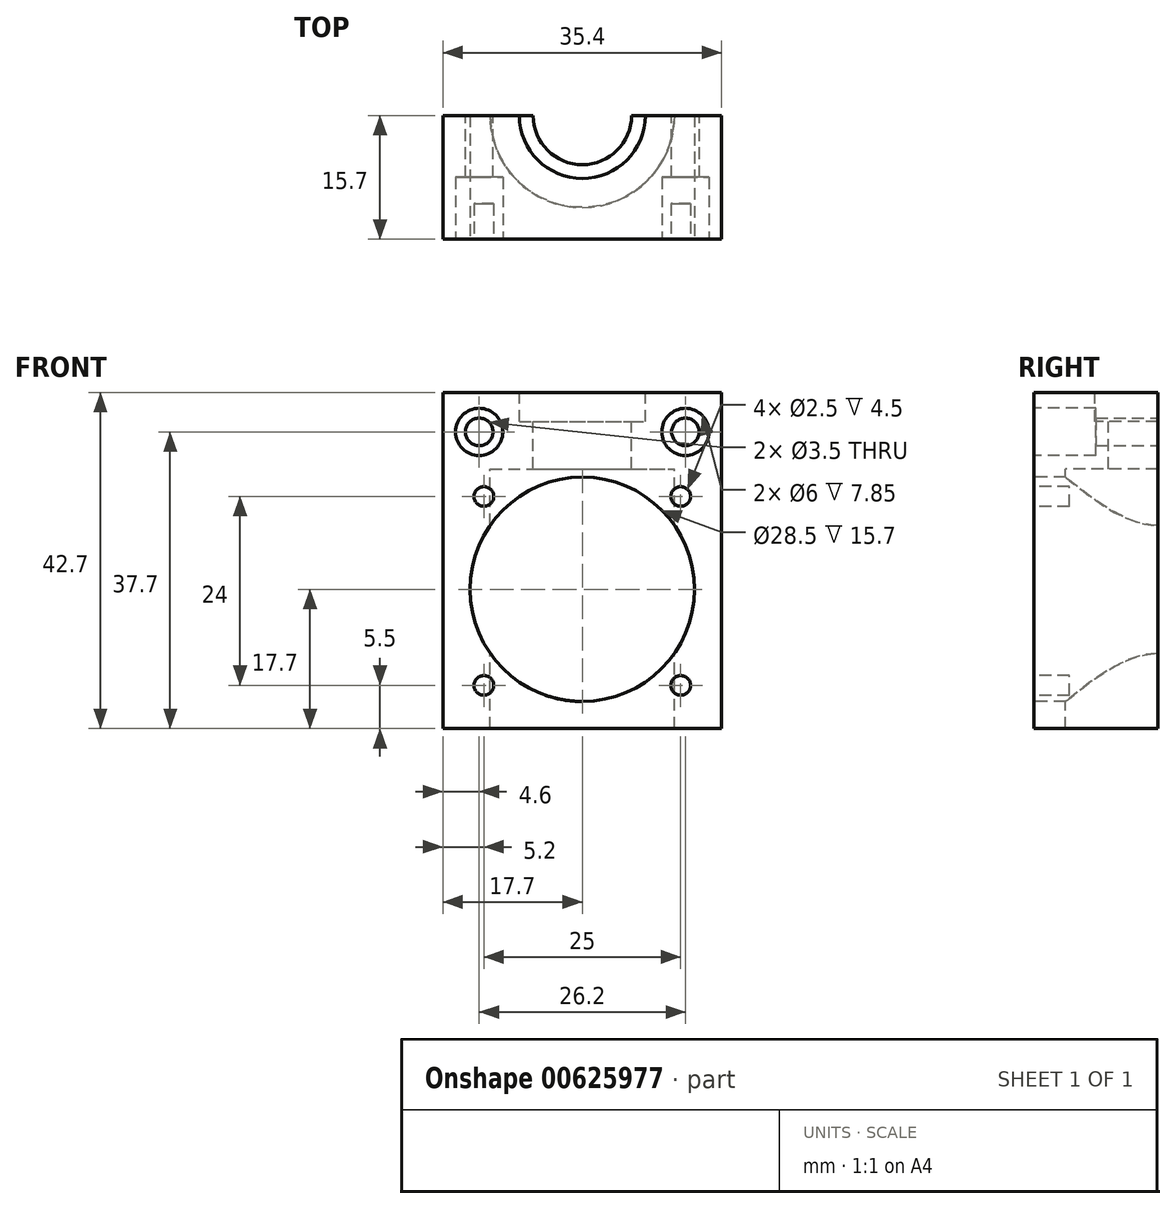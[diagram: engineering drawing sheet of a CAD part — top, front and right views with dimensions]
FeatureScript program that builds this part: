
annotation { "Feature Type Name" : "Feature", "Feature Type Description" : "" }
export const myFeature = defineFeature(function(context is Context, id is Id, definition is map)
    precondition{}
    {
        {
            var Q0;
            Q0=qCreatedBy(makeId("Top.planeOp"),FACE);
            var sketch = newSketch(context, id + "F0", { "sketchPlane" : qUnion([Q0])});
            skLineSegment(sketch, "E0.bottom", {"start": v(0, 0) * mm, "end": v(35.4, 0) * mm});
            skLineSegment(sketch, "E0.top", {"start": v(0, 15.7) * mm, "end": v(35.4, 15.7) * mm});
            skLineSegment(sketch, "E0.left", {"start": v(0, 0) * mm, "end": v(0, 15.7) * mm});
            skLineSegment(sketch, "E0.right", {"start": v(35.4, 0) * mm, "end": v(35.4, 15.7) * mm});
            skSolve(sketch);
        }
        {
            var Q0;
            Q0=makeQuery(id+"F0.imprint","IMPRINT",FACE,{"disambiguationData":[TD([[makeQuery(id+"F0.imprint","IMPRINT",EDGE,{"derivedFrom":sQuery(id+"F0.wireOp",EDGE,"E0.bottom")}),1.0]])]});
            extrude(context, id + "F1", {"entities" : qUnion([Q0]), "depth" : 42.7 * mm, "offsetDistance" : 25 * mm});
        }
        {
            var Q0;
            Q0=makeQuery(id+"F1.opExtrude","CAP_FACE",FACE,{"disambiguationData":[OSD([sQuery(id+"F0.wireOp",EDGE,"E0.bottom"),sQuery(id+"F0.wireOp",EDGE,"E0.top"),sQuery(id+"F0.wireOp",EDGE,"E0.left"),sQuery(id+"F0.wireOp",EDGE,"E0.right")])],"isStart":false});
            var sketch = newSketch(context, id + "F2", { "sketchPlane" : qUnion([Q0])});
            skCircle(sketch, "E1", {"center": v(17.7, 15.7) * mm, "radius": 8 * mm});
            skSolve(sketch);
        }
        {
            var Q0;
            {var subQ0=sQuery(id+"F2.wireOp",EDGE,"E1");var subQ1=makeQuery(id+"F1.opExtrude","CAP_EDGE",EDGE,{"disambiguationData":[OSD([sQuery(id+"F0.wireOp",EDGE,"E0.top")])],"isStart":false});var subQ2=makeQuery(id+"F2.imprint","INTERSECT",VERTEX,{"disambiguationData":[OD(0.0)],"derivedFrom":[subQ1,subQ0]});Q0=makeQuery(id+"F2.imprint","IMPRINT",FACE,{"disambiguationData":[TD([[makeQuery(id+"F2.imprint","IMPRINT",EDGE,{"disambiguationData":[TD([[subQ2,-1.0]])],"derivedFrom":subQ0}),1.0]])]});}
            extrude(context, id + "F3", {"entities" : qUnion([Q0]), "operationType" : NewBodyOperationType.REMOVE, "oppositeDirection" : true, "depth" : 3.7 * mm, "offsetDistance" : 25 * mm});
        }
        {
            var Q0;
            Q0=makeQuery(id+"F3.boolean.opBoolean","COPY",FACE,{"derivedFrom":makeQuery(id+"F3.opExtrude","CAP_FACE",FACE,{"disambiguationData":[OSD([sQuery(id+"F0.wireOp",EDGE,"E0.top"),sQuery(id+"F2.wireOp",EDGE,"E1")])],"isStart":false})});
            var sketch = newSketch(context, id + "F4", { "sketchPlane" : qUnion([Q0])});
            skCircle(sketch, "E2", {"center": v(17.7, 15.7) * mm, "radius": 6.25 * mm});
            skSolve(sketch);
        }
        {
            var Q0;
            {var subQ0=sQuery(id+"F4.wireOp",EDGE,"E2");var subQ1=makeQuery(id+"F3.boolean.opBoolean","COPY",EDGE,{"derivedFrom":makeQuery(id+"F3.opExtrude","CAP_EDGE",EDGE,{"disambiguationData":[OSD([sQuery(id+"F0.wireOp",EDGE,"E0.top")])],"isStart":false})});var subQ2=makeQuery(id+"F4.imprint","INTERSECT",VERTEX,{"disambiguationData":[OD(0.0)],"derivedFrom":[subQ1,subQ0]});Q0=makeQuery(id+"F4.imprint","IMPRINT",FACE,{"disambiguationData":[TD([[makeQuery(id+"F4.imprint","IMPRINT",EDGE,{"disambiguationData":[TD([[subQ2,-1.0]])],"derivedFrom":subQ0}),1.0]])]});}
            extrude(context, id + "F5", {"entities" : qUnion([Q0]), "operationType" : NewBodyOperationType.REMOVE, "oppositeDirection" : true, "depth" : 6 * mm, "offsetDistance" : 25 * mm});
        }
        {
            var Q0;
            Q0=makeQuery(id+"F5.boolean.opBoolean","COPY",FACE,{"derivedFrom":makeQuery(id+"F5.opExtrude","CAP_FACE",FACE,{"disambiguationData":[OSD([sQuery(id+"F0.wireOp",EDGE,"E0.top"),sQuery(id+"F4.wireOp",EDGE,"E2")])],"isStart":false})});
            var sketch = newSketch(context, id + "F6", { "sketchPlane" : qUnion([Q0])});
            skCircle(sketch, "E3", {"center": v(17.7, 15.7) * mm, "radius": 11.7 * mm});
            skSolve(sketch);
        }
        {
            var Q0;
            Q0=makeQuery(id+"F6.imprint","IMPRINT",FACE,{"disambiguationData":[TD([[makeQuery(id+"F6.imprint","IMPRINT",EDGE,{"derivedFrom":makeQuery(id+"F5.boolean.opBoolean","COPY",EDGE,{"derivedFrom":makeQuery(id+"F5.opExtrude","CAP_EDGE",EDGE,{"disambiguationData":[OSD([sQuery(id+"F4.wireOp",EDGE,"E2")])],"isStart":false})})}),1.0]])]});
            var Q1;
            Q1=makeQuery(id+"F6.imprint","IMPRINT",FACE,{"disambiguationData":[TD([[makeQuery(id+"F6.imprint","IMPRINT",EDGE,{"derivedFrom":sQuery(id+"F6.wireOp",EDGE,"E3")}),1.0]])]});
            extrude(context, id + "F7", {"entities" : qUnion([Q0, Q1]), "operationType" : NewBodyOperationType.REMOVE, "oppositeDirection" : true, "depth" : 35 * mm, "offsetDistance" : 25 * mm});
        }
        {
            var Q0;
            Q0=makeQuery(id+"F1.opExtrude","SWEPT_FACE",FACE,{"disambiguationData":[OSD([sQuery(id+"F0.wireOp",EDGE,"E0.bottom")])]});
            var sketch = newSketch(context, id + "F8", { "sketchPlane" : qUnion([Q0])});
            skCircle(sketch, "E4", {"center": v(17.7, 17.7) * mm, "radius": 14.25 * mm});
            skPoint(sketch, "E5.centerSnap0", {"position": v(35.4, 21.35) * mm});
            skSolve(sketch);
        }
        {
            var Q0;
            Q0 = qSketchRegion(id + "F8", true);
            extrude(context, id + "F9", {"entities" : qUnion([Q0]), "operationType" : NewBodyOperationType.REMOVE, "oppositeDirection" : true, "depth" : 25 * mm, "offsetDistance" : 25 * mm});
        }
        {
            var Q0;
            Q0=makeQuery(id+"F1.opExtrude","SWEPT_FACE",FACE,{"disambiguationData":[OSD([sQuery(id+"F0.wireOp",EDGE,"E0.bottom")])]});
            var sketch = newSketch(context, id + "F10", { "sketchPlane" : qUnion([Q0])});
            skCircle(sketch, "E6", {"center": v(5.2, 29.5) * mm, "radius": 1.25 * mm});
            skCircle(sketch, "E7", {"center": v(30.2, 29.5) * mm, "radius": 1.25 * mm});
            skCircle(sketch, "E8", {"center": v(30.2, 5.5) * mm, "radius": 1.25 * mm});
            skCircle(sketch, "E9", {"center": v(5.2, 5.5) * mm, "radius": 1.25 * mm});
            skSolve(sketch);
        }
        {
            var Q0;
            Q0=makeQuery(id+"F10.imprint","IMPRINT",FACE,{"disambiguationData":[TD([[makeQuery(id+"F10.imprint","IMPRINT",EDGE,{"derivedFrom":sQuery(id+"F10.wireOp",EDGE,"E9")}),1.0]])]});
            var Q1;
            Q1=makeQuery(id+"F10.imprint","IMPRINT",FACE,{"disambiguationData":[TD([[makeQuery(id+"F10.imprint","IMPRINT",EDGE,{"derivedFrom":sQuery(id+"F10.wireOp",EDGE,"E6")}),1.0]])]});
            var Q2;
            Q2=makeQuery(id+"F10.imprint","IMPRINT",FACE,{"disambiguationData":[TD([[makeQuery(id+"F10.imprint","IMPRINT",EDGE,{"derivedFrom":sQuery(id+"F10.wireOp",EDGE,"E7")}),1.0]])]});
            var Q3;
            Q3=makeQuery(id+"F10.imprint","IMPRINT",FACE,{"disambiguationData":[TD([[makeQuery(id+"F10.imprint","IMPRINT",EDGE,{"derivedFrom":sQuery(id+"F10.wireOp",EDGE,"E8")}),1.0]])]});
            extrude(context, id + "F11", {"entities" : qUnion([Q0, Q1, Q2, Q3]), "operationType" : NewBodyOperationType.REMOVE, "oppositeDirection" : true, "depth" : 4.5 * mm, "offsetDistance" : 25 * mm});
        }
        {
            var Q0;
            {var subQ1=sQuery(id+"F0.wireOp",EDGE,"E0.right");var subQ3=sQuery(id+"F0.wireOp",EDGE,"E0.top");Q0=makeQuery(id+"F7.boolean.opBoolean","SPLIT",FACE,{"disambiguationData":[TD([makeQuery(id+"F1.opExtrude","SWEPT_FACE",FACE,{"disambiguationData":[OSD([subQ1])]})])],"derivedFrom":makeQuery(id+"F1.opExtrude","SWEPT_FACE",FACE,{"disambiguationData":[OSD([subQ3])]})});}
            var sketch = newSketch(context, id + "F12", { "sketchPlane" : qUnion([Q0])});
            skCircle(sketch, "E10", {"center": v(-30.8, 37.7) * mm, "radius": 1.75 * mm});
            skCircle(sketch, "E11", {"center": v(-4.6, 37.7) * mm, "radius": 1.75 * mm});
            skSolve(sketch);
        }
        {
            var Q0;
            Q0=makeQuery(id+"F12.imprint","IMPRINT",FACE,{"disambiguationData":[TD([[makeQuery(id+"F12.imprint","IMPRINT",EDGE,{"derivedFrom":sQuery(id+"F12.wireOp",EDGE,"E11")}),1.0]])]});
            var Q1;
            Q1=makeQuery(id+"F12.imprint","IMPRINT",FACE,{"disambiguationData":[TD([[makeQuery(id+"F12.imprint","IMPRINT",EDGE,{"derivedFrom":sQuery(id+"F12.wireOp",EDGE,"E10")}),1.0]])]});
            extrude(context, id + "F13", {"entities" : qUnion([Q0, Q1]), "operationType" : NewBodyOperationType.REMOVE, "oppositeDirection" : true, "depth" : 25 * mm, "offsetDistance" : 25 * mm});
        }
        {
            var Q0;
            Q0=makeQuery(id+"F1.opExtrude","SWEPT_FACE",FACE,{"disambiguationData":[OSD([sQuery(id+"F0.wireOp",EDGE,"E0.bottom")])]});
            var sketch = newSketch(context, id + "F14", { "sketchPlane" : qUnion([Q0])});
            skCircle(sketch, "E12", {"center": v(4.6, 37.7) * mm, "radius": 3 * mm});
            skCircle(sketch, "E13", {"center": v(30.8, 37.7) * mm, "radius": 3 * mm});
            skSolve(sketch);
        }
        {
            var Q0;
            Q0=makeQuery(id+"F14.imprint","IMPRINT",FACE,{"disambiguationData":[TD([[makeQuery(id+"F14.imprint","IMPRINT",EDGE,{"derivedFrom":sQuery(id+"F14.wireOp",EDGE,"E12")}),1.0]])]});
            var Q1;
            Q1=makeQuery(id+"F14.imprint","IMPRINT",FACE,{"disambiguationData":[TD([[makeQuery(id+"F14.imprint","IMPRINT",EDGE,{"derivedFrom":sQuery(id+"F14.wireOp",EDGE,"E13")}),1.0]])]});
            extrude(context, id + "F15", {"entities" : qUnion([Q0, Q1]), "operationType" : NewBodyOperationType.REMOVE, "oppositeDirection" : true, "depth" : 7.85 * mm, "offsetDistance" : 25 * mm});
        }
    });
